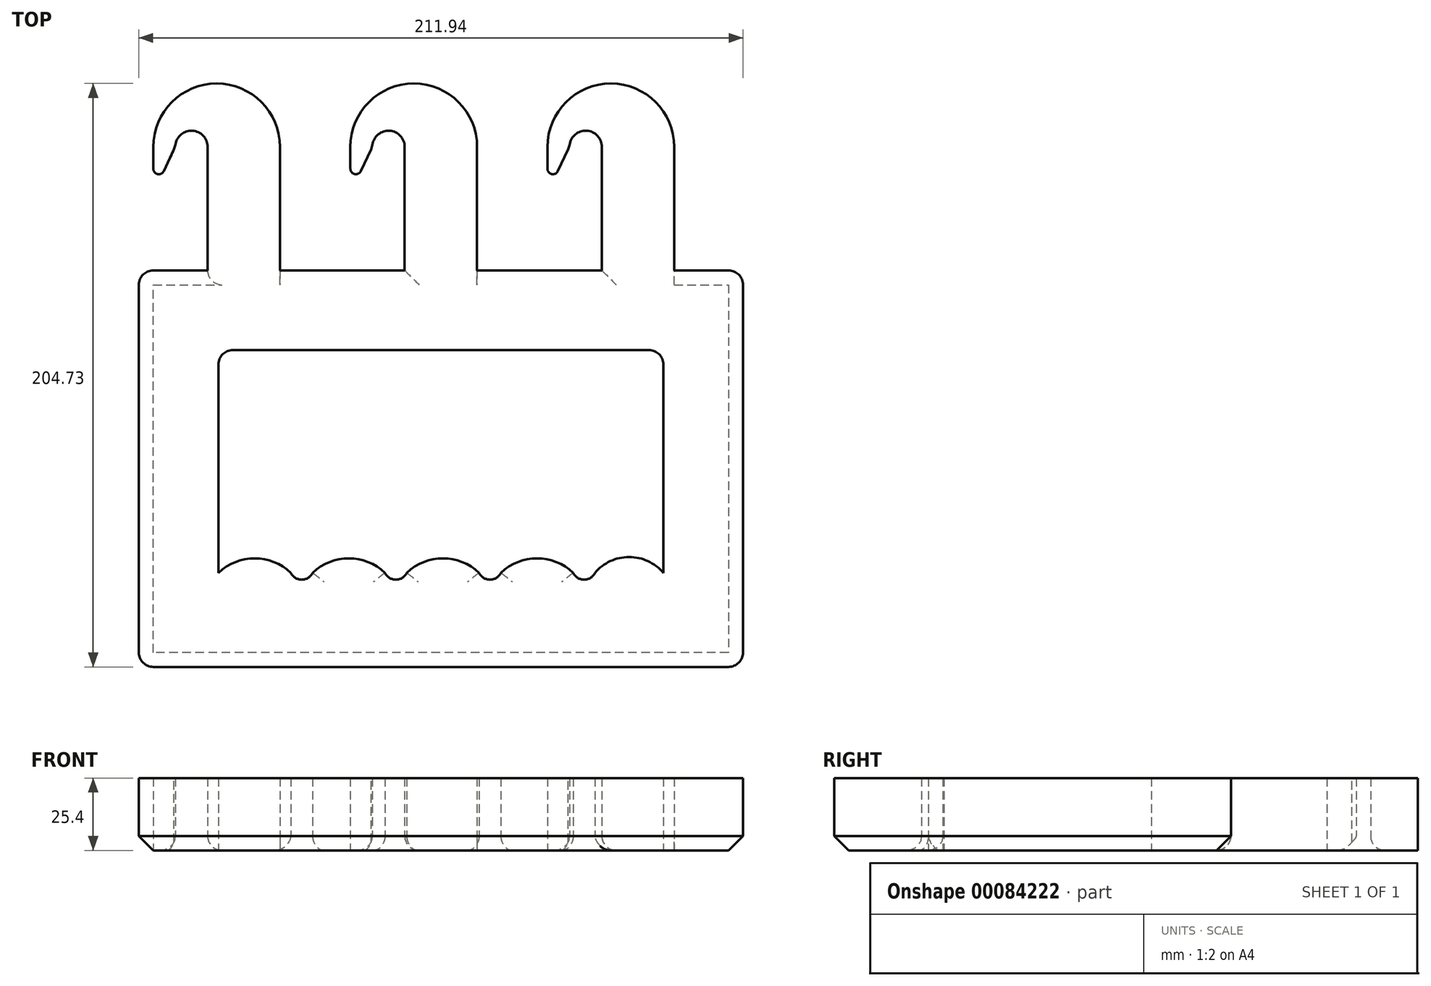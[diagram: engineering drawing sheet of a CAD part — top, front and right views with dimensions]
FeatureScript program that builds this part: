
annotation { "Feature Type Name" : "Feature", "Feature Type Description" : "" }
export const myFeature = defineFeature(function(context is Context, id is Id, definition is map)
    precondition{}
    {
        {
            var Q0;
            Q0=qCreatedBy(makeId("Top.planeOp"),FACE);
            var sketch = newSketch(context, id + "F0", { "sketchPlane" : qUnion([Q0])});
            skLineSegment(sketch, "E0.bottom", {"start": v(80.57, 44.18) * mm, "end": v(-80.57, 44.18) * mm});
            skLineSegment(sketch, "E0.top", {"start": v(80.57, -44.18) * mm, "end": v(-80.57, -44.18) * mm});
            skLineSegment(sketch, "E0.left", {"start": v(80.57, 44.18) * mm, "end": v(80.57, -44.18) * mm});
            skLineSegment(sketch, "E0.right", {"start": v(-80.57, 44.18) * mm, "end": v(-80.57, -44.18) * mm});
            skPoint(sketch, "E0.middle", {"position": v(0, 0) * mm});
            skSolve(sketch);
        }
        {
            var Q0;
            Q0=makeQuery(id+"F0.imprint","IMPRINT",FACE,{"disambiguationData":[TD([[makeQuery(id+"F0.imprint","IMPRINT",EDGE,{"derivedFrom":sQuery(id+"F0.wireOp",EDGE,"E0.bottom")}),1.0]])]});
            extrude(context, id + "F1", {"entities" : qUnion([Q0]), "depth" : 25.4 * mm});
        }
        {
            var Q0;
            Q0=makeQuery(id+"F1.opExtrude","CAP_FACE",FACE,{"disambiguationData":[OSD([sQuery(id+"F0.wireOp",EDGE,"E0.bottom"),sQuery(id+"F0.wireOp",EDGE,"E0.top"),sQuery(id+"F0.wireOp",EDGE,"E0.left"),sQuery(id+"F0.wireOp",EDGE,"E0.right")])],"isStart":true});
            var Q1;
            Q1=makeQuery(id+"F1.opExtrude","CAP_FACE",FACE,{"disambiguationData":[OSD([sQuery(id+"F0.wireOp",EDGE,"E0.bottom"),sQuery(id+"F0.wireOp",EDGE,"E0.top"),sQuery(id+"F0.wireOp",EDGE,"E0.left"),sQuery(id+"F0.wireOp",EDGE,"E0.right")])],"isStart":false});
            shell(context, id + "F2", {"entities" : qUnion([Q0, Q1]), "thickness" : 2.54 * mm});
        }
        {
            var Q0;
            Q0=makeQuery(id+"F1.opExtrude","SWEPT_FACE",FACE,{"disambiguationData":[OSD([sQuery(id+"F0.wireOp",EDGE,"E0.top")])]});
            extrude(context, id + "F3", {"entities" : qUnion([Q0]), "operationType" : NewBodyOperationType.ADD, "depth" : 25.4 * mm});
        }
        {
            var Q0;
            {var subQ0=sQuery(id+"F0.wireOp",EDGE,"E0.left");Q0=makeQuery(id+"F3.boolean.opBoolean","MERGE",FACE,{"derivedFrom":[makeQuery(id+"F1.opExtrude","SWEPT_FACE",FACE,{"disambiguationData":[OSD([subQ0])]}),makeQuery(id+"F3.opExtrude","SWEPT_FACE",FACE,{"disambiguationData":[OSD([sQuery(id+"F0.wireOp",EDGE,"E0.top"),subQ0])]})]});}
            extrude(context, id + "F4", {"entities" : qUnion([Q0]), "operationType" : NewBodyOperationType.ADD, "depth" : 25.4 * mm});
        }
        {
            var Q0;
            {var subQ0=sQuery(id+"F0.wireOp",EDGE,"E0.bottom");Q0=makeQuery(id+"F4.boolean.opBoolean","MERGE",FACE,{"derivedFrom":[makeQuery(id+"F1.opExtrude","SWEPT_FACE",FACE,{"disambiguationData":[OSD([subQ0])]}),makeQuery(id+"F4.opExtrude","SWEPT_FACE",FACE,{"disambiguationData":[OSD([subQ0,sQuery(id+"F0.wireOp",EDGE,"E0.left")])]})]});}
            extrude(context, id + "F5", {"entities" : qUnion([Q0]), "operationType" : NewBodyOperationType.ADD, "depth" : 25.4 * mm});
        }
        {
            var Q0;
            {var subQ0=sQuery(id+"F0.wireOp",EDGE,"E0.right");Q0=makeQuery(id+"F5.boolean.opBoolean","MERGE",FACE,{"derivedFrom":[makeQuery(id+"F3.boolean.opBoolean","MERGE",FACE,{"derivedFrom":[makeQuery(id+"F1.opExtrude","SWEPT_FACE",FACE,{"disambiguationData":[OSD([subQ0])]}),makeQuery(id+"F3.opExtrude","SWEPT_FACE",FACE,{"disambiguationData":[OSD([sQuery(id+"F0.wireOp",EDGE,"E0.top"),subQ0])]})]}),makeQuery(id+"F5.opExtrude","SWEPT_FACE",FACE,{"disambiguationData":[OSD([sQuery(id+"F0.wireOp",EDGE,"E0.bottom"),subQ0])]})]});}
            extrude(context, id + "F6", {"entities" : qUnion([Q0]), "operationType" : NewBodyOperationType.ADD, "depth" : 25.4 * mm});
        }
        {
            var Q0;
            Q0=makeQuery(id+"F6.opExtrude","CAP_EDGE",EDGE,{"disambiguationData":[OSD([sQuery(id+"F0.wireOp",EDGE,"E0.top"),sQuery(id+"F0.wireOp",EDGE,"E0.right")])],"isStart":false});
            var Q1;
            Q1=makeQuery(id+"F2.opShell","OFFSET_EDGE",EDGE,{"disambiguationData":[OSD([sQuery(id+"F0.wireOp",EDGE,"E0.top"),sQuery(id+"F0.wireOp",EDGE,"E0.right")])]});
            var Q2;
            {var subQ0=sQuery(id+"F0.wireOp",EDGE,"E0.left");var subQ1=sQuery(id+"F0.wireOp",EDGE,"E0.bottom");Q2=makeQuery(id+"F5.opExtrude","CAP_EDGE",EDGE,{"disambiguationData":[OSD([subQ1,subQ0]),TDD([makeQuery(id+"F4.opExtrude","CAP_EDGE",EDGE,{"disambiguationData":[OSD([subQ1,subQ0])],"isStart":false})])],"isStart":false});}
            var Q3;
            Q3=makeQuery(id+"F6.opExtrude","CAP_EDGE",EDGE,{"disambiguationData":[OSD([sQuery(id+"F0.wireOp",EDGE,"E0.bottom"),sQuery(id+"F0.wireOp",EDGE,"E0.right")])],"isStart":false});
            var Q4;
            Q4=makeQuery(id+"F2.opShell","OFFSET_EDGE",EDGE,{"disambiguationData":[OSD([sQuery(id+"F0.wireOp",EDGE,"E0.bottom"),sQuery(id+"F0.wireOp",EDGE,"E0.right")])]});
            var Q5;
            Q5=makeQuery(id+"F2.opShell","OFFSET_EDGE",EDGE,{"disambiguationData":[OSD([sQuery(id+"F0.wireOp",EDGE,"E0.bottom"),sQuery(id+"F0.wireOp",EDGE,"E0.left")])]});
            var Q6;
            Q6=makeQuery(id+"F2.opShell","OFFSET_EDGE",EDGE,{"disambiguationData":[OSD([sQuery(id+"F0.wireOp",EDGE,"E0.top"),sQuery(id+"F0.wireOp",EDGE,"E0.left")])]});
            var Q7;
            {var subQ0=sQuery(id+"F0.wireOp",EDGE,"E0.left");var subQ1=sQuery(id+"F0.wireOp",EDGE,"E0.top");Q7=makeQuery(id+"F4.opExtrude","CAP_EDGE",EDGE,{"disambiguationData":[OSD([subQ1,subQ0]),TDD([makeQuery(id+"F3.opExtrude","CAP_EDGE",EDGE,{"disambiguationData":[OSD([subQ1,subQ0])],"isStart":false})])],"isStart":false});}
            fillet(context, id + "F7", {"entities" : qUnion([Q0, Q1, Q2, Q3, Q4, Q5, Q6, Q7]), "radius" : 5.08 * mm, "tangentPropagation" : true, "allowEdgeOverflow" : false});
        }
        {
            var Q0;
            {var subQ0=sQuery(id+"F0.wireOp",EDGE,"E0.right");var subQ1=sQuery(id+"F0.wireOp",EDGE,"E0.left");var subQ2=sQuery(id+"F0.wireOp",EDGE,"E0.top");var subQ3=sQuery(id+"F0.wireOp",EDGE,"E0.bottom");Q0=makeQuery(id+"F4rlxRPwf46HhCo_1.boolean.opBoolean","MERGE",FACE,{"derivedFrom":[makeQuery(id+"F6.boolean.opBoolean","MERGE",FACE,{"derivedFrom":[makeQuery(id+"F5.boolean.opBoolean","MERGE",FACE,{"derivedFrom":[makeQuery(id+"F4.boolean.opBoolean","MERGE",FACE,{"derivedFrom":[makeQuery(id+"F3.boolean.opBoolean","MERGE",FACE,{"derivedFrom":[makeQuery(id+"F1.opExtrude","CAP_FACE",FACE,{"disambiguationData":[OSD([subQ3,subQ2,subQ1,subQ0])],"isStart":true}),makeQuery(id+"F3.opExtrude","SWEPT_FACE",FACE,{"disambiguationData":[OSD([subQ2]),TDD([makeQuery(id+"F1.opExtrude","CAP_EDGE",EDGE,{"disambiguationData":[OSD([subQ2])],"isStart":true})])]})]}),makeQuery(id+"F4.opExtrude","SWEPT_FACE",FACE,{"disambiguationData":[OSD([subQ2,subQ1]),TDD([makeQuery(id+"F3.boolean.opBoolean","MERGE",EDGE,{"derivedFrom":[makeQuery(id+"F1.opExtrude","CAP_EDGE",EDGE,{"disambiguationData":[OSD([subQ1])],"isStart":true}),makeQuery(id+"F3.opExtrude","SWEPT_EDGE",EDGE,{"disambiguationData":[OSD([subQ2,subQ1]),TDD([makeQuery(id+"F1.opExtrude","CAP_VERTEX",VERTEX,{"disambiguationData":[OSD([subQ2,subQ1])],"isStart":true})])]})]})])]})]}),makeQuery(id+"F5.opExtrude","SWEPT_FACE",FACE,{"disambiguationData":[OSD([subQ3,subQ1]),TDD([makeQuery(id+"F4.boolean.opBoolean","MERGE",EDGE,{"derivedFrom":[makeQuery(id+"F1.opExtrude","CAP_EDGE",EDGE,{"disambiguationData":[OSD([subQ3])],"isStart":true}),makeQuery(id+"F4.opExtrude","SWEPT_EDGE",EDGE,{"disambiguationData":[OSD([subQ3,subQ1]),TDD([makeQuery(id+"F1.opExtrude","CAP_VERTEX",VERTEX,{"disambiguationData":[OSD([subQ3,subQ1])],"isStart":true})])]})]})])]})]}),makeQuery(id+"F6.opExtrude","SWEPT_FACE",FACE,{"disambiguationData":[OSD([subQ3,subQ2,subQ0]),TDD([makeQuery(id+"F5.boolean.opBoolean","MERGE",EDGE,{"derivedFrom":[makeQuery(id+"F3.boolean.opBoolean","MERGE",EDGE,{"derivedFrom":[makeQuery(id+"F1.opExtrude","CAP_EDGE",EDGE,{"disambiguationData":[OSD([subQ0])],"isStart":true}),makeQuery(id+"F3.opExtrude","SWEPT_EDGE",EDGE,{"disambiguationData":[OSD([subQ2,subQ0]),TDD([makeQuery(id+"F1.opExtrude","CAP_VERTEX",VERTEX,{"disambiguationData":[OSD([subQ2,subQ0])],"isStart":true})])]})]}),makeQuery(id+"F5.opExtrude","SWEPT_EDGE",EDGE,{"disambiguationData":[OSD([subQ3,subQ0]),TDD([makeQuery(id+"F1.opExtrude","CAP_VERTEX",VERTEX,{"disambiguationData":[OSD([subQ3,subQ0])],"isStart":true})])]})]})])]})]}),makeQuery(id+"F4rlxRPwf46HhCo_1.opExtrude","CAP_FACE",FACE,{"disambiguationData":[OSD([subQ3,subQ2,subQ1,subQ0,sQuery(id+"FdWGWdMTT6Qc4Fu_1.wireOp",EDGE,"d3da10bc-3136-4792-8693-016e846191d0"),sQuery(id+"FdWGWdMTT6Qc4Fu_1.wireOp",EDGE,"aac24d95-50fc-4f8b-b2ee-a3f1f59186e0"),sQuery(id+"FdWGWdMTT6Qc4Fu_1.wireOp",EDGE,"4d405499-a267-42fc-9aab-180142b3633d"),sQuery(id+"FdWGWdMTT6Qc4Fu_1.wireOp",EDGE,"a9ec6842-2591-4f58-a969-2822cd4d4c04"),sQuery(id+"FdWGWdMTT6Qc4Fu_1.wireOp",EDGE,"51de34cb-b12d-4a25-9cfc-016ff7969eb1"),sQuery(id+"FdWGWdMTT6Qc4Fu_1.wireOp",EDGE,"a70d7e88-b675-4396-b805-becb8ebd9cdd"),sQuery(id+"FdWGWdMTT6Qc4Fu_1.wireOp",EDGE,"c629b940-030e-440d-8414-086baef94262"),sQuery(id+"FdWGWdMTT6Qc4Fu_1.wireOp",EDGE,"5c281ef1-6288-44ce-9a01-84a85776ec3e"),sQuery(id+"FdWGWdMTT6Qc4Fu_1.wireOp",EDGE,"403098cf-f73b-4ddd-90e9-7737bff6dcb0")])],"isStart":true})]});}
            var sketch = newSketch(context, id + "F8", { "sketchPlane" : qUnion([Q0])});
            skLineSegment(sketch, "E1.bottom", {"start": v(-81.84, -69.58) * mm, "end": v(-56.44, -69.58) * mm});
            skLineSegment(sketch, "E1.top", {"start": v(-81.84, -112.92) * mm, "end": v(-56.44, -112.92) * mm});
            skLineSegment(sketch, "E1.left", {"start": v(-81.84, -69.58) * mm, "end": v(-81.84, -112.92) * mm});
            skLineSegment(sketch, "E1.right", {"start": v(-56.44, -69.58) * mm, "end": v(-56.44, -112.92) * mm});
            skLineSegment(sketch, "E2.bottom", {"start": v(81.84, -69.58) * mm, "end": v(56.44, -69.58) * mm});
            skLineSegment(sketch, "E2.top", {"start": v(81.84, -112.92) * mm, "end": v(56.44, -112.92) * mm});
            skLineSegment(sketch, "E2.left", {"start": v(81.84, -69.58) * mm, "end": v(81.84, -112.92) * mm});
            skLineSegment(sketch, "E2.right", {"start": v(56.44, -69.58) * mm, "end": v(56.44, -112.92) * mm});
            skLineSegment(sketch, "E3.bottom", {"start": v(-12.7, -69.58) * mm, "end": v(12.7, -69.58) * mm});
            skLineSegment(sketch, "E3.top", {"start": v(-12.7, -112.92) * mm, "end": v(12.7, -112.92) * mm});
            skLineSegment(sketch, "E3.left", {"start": v(-12.7, -69.58) * mm, "end": v(-12.7, -112.92) * mm});
            skLineSegment(sketch, "E3.right", {"start": v(12.7, -69.58) * mm, "end": v(12.7, -112.92) * mm});
            skArc(sketch, "E4", {"start": v(-100.9, -112.92) * mm, "mid": v(-78.67, -135.15) * mm, "end": v(-56.44, -112.92) * mm});
            skArc(sketch, "E5", {"start": v(-31.75, -112.92) * mm, "mid": v(-9.52, -135.15) * mm, "end": v(12.7, -112.92) * mm});
            skArc(sketch, "E6", {"start": v(37.4, -112.92) * mm, "mid": v(59.62, -135.15) * mm, "end": v(81.84, -112.92) * mm});
            skPoint(sketch, "E6.startSnap0", {"position": v(69.14, -112.92) * mm});
            skLineSegment(sketch, "E7", {"start": v(-100.9, -112.92) * mm, "end": v(-100.9, -96.82) * mm});
            skLineSegment(sketch, "E8", {"start": v(-31.75, -112.92) * mm, "end": v(-31.75, -96.82) * mm});
            skLineSegment(sketch, "E9", {"start": v(37.4, -112.92) * mm, "end": v(37.4, -96.82) * mm});
            skLineSegment(sketch, "E10", {"start": v(-100.9, -96.82) * mm, "end": v(-93.19, -112.92) * mm});
            skLineSegment(sketch, "E11", {"start": v(-31.75, -96.82) * mm, "end": v(-24.05, -112.92) * mm});
            skLineSegment(sketch, "E12", {"start": v(37.4, -96.82) * mm, "end": v(45.09, -112.92) * mm});
            skArc(sketch, "E13", {"start": v(-93.19, -112.92) * mm, "mid": v(-87.51, -118.6) * mm, "end": v(-81.84, -112.92) * mm});
            skArc(sketch, "E14", {"start": v(-24.05, -112.92) * mm, "mid": v(-18.37, -118.6) * mm, "end": v(-12.7, -112.92) * mm});
            skArc(sketch, "E15", {"start": v(45.09, -112.92) * mm, "mid": v(50.76, -118.6) * mm, "end": v(56.44, -112.92) * mm});
            skSolve(sketch);
        }
        {
            var Q0;
            Q0=makeQuery(id+"F8.imprint","IMPRINT",FACE,{"disambiguationData":[TD([[makeQuery(id+"F8.imprint","IMPRINT",EDGE,{"derivedFrom":sQuery(id+"F8.wireOp",EDGE,"E1.top")}),-1.0]])]});
            var Q1;
            Q1=makeQuery(id+"F8.imprint","IMPRINT",FACE,{"disambiguationData":[TD([[makeQuery(id+"F8.imprint","IMPRINT",EDGE,{"derivedFrom":sQuery(id+"F8.wireOp",EDGE,"E1.bottom")}),1.0]])]});
            var Q2;
            Q2=makeQuery(id+"F8.imprint","IMPRINT",FACE,{"disambiguationData":[TD([[makeQuery(id+"F8.imprint","IMPRINT",EDGE,{"derivedFrom":sQuery(id+"F8.wireOp",EDGE,"E2.top")}),1.0]])]});
            var Q3;
            Q3=makeQuery(id+"F8.imprint","IMPRINT",FACE,{"disambiguationData":[TD([[makeQuery(id+"F8.imprint","IMPRINT",EDGE,{"derivedFrom":sQuery(id+"F8.wireOp",EDGE,"E3.bottom")}),1.0]])]});
            var Q4;
            Q4=makeQuery(id+"F8.imprint","IMPRINT",FACE,{"disambiguationData":[TD([[makeQuery(id+"F8.imprint","IMPRINT",EDGE,{"derivedFrom":sQuery(id+"F8.wireOp",EDGE,"E2.bottom")}),1.0]])]});
            var Q5;
            Q5=makeQuery(id+"F8.imprint","IMPRINT",FACE,{"disambiguationData":[TD([[makeQuery(id+"F8.imprint","IMPRINT",EDGE,{"derivedFrom":sQuery(id+"F8.wireOp",EDGE,"E3.top")}),-1.0]])]});
            extrude(context, id + "F9", {"entities" : qUnion([Q0, Q1, Q2, Q3, Q4, Q5]), "operationType" : NewBodyOperationType.ADD, "oppositeDirection" : true, "depth" : 25.4 * mm});
        }
        {
            var Q0;
            {var subQ0=sQuery(id+"F0.wireOp",EDGE,"E0.right");var subQ1=sQuery(id+"F0.wireOp",EDGE,"E0.bottom");var subQ2=sQuery(id+"F0.wireOp",EDGE,"E0.top");var subQ3=sQuery(id+"F0.wireOp",EDGE,"E0.left");Q0=makeQuery(id+"F9.boolean.opBoolean","MERGE",FACE,{"derivedFrom":[makeQuery(id+"F6.boolean.opBoolean","MERGE",FACE,{"derivedFrom":[makeQuery(id+"F5.boolean.opBoolean","MERGE",FACE,{"derivedFrom":[makeQuery(id+"F4.boolean.opBoolean","MERGE",FACE,{"derivedFrom":[makeQuery(id+"F3.boolean.opBoolean","MERGE",FACE,{"derivedFrom":[makeQuery(id+"F1.opExtrude","CAP_FACE",FACE,{"disambiguationData":[OSD([subQ1,subQ2,subQ3,subQ0])],"isStart":true}),makeQuery(id+"F3.opExtrude","SWEPT_FACE",FACE,{"disambiguationData":[OSD([subQ2]),TDD([makeQuery(id+"F1.opExtrude","CAP_EDGE",EDGE,{"disambiguationData":[OSD([subQ2])],"isStart":true})])]})]}),makeQuery(id+"F4.opExtrude","SWEPT_FACE",FACE,{"disambiguationData":[OSD([subQ2,subQ3]),TDD([makeQuery(id+"F3.boolean.opBoolean","MERGE",EDGE,{"derivedFrom":[makeQuery(id+"F1.opExtrude","CAP_EDGE",EDGE,{"disambiguationData":[OSD([subQ3])],"isStart":true}),makeQuery(id+"F3.opExtrude","SWEPT_EDGE",EDGE,{"disambiguationData":[OSD([subQ2,subQ3]),TDD([makeQuery(id+"F1.opExtrude","CAP_VERTEX",VERTEX,{"disambiguationData":[OSD([subQ2,subQ3])],"isStart":true})])]})]})])]})]}),makeQuery(id+"F5.opExtrude","SWEPT_FACE",FACE,{"disambiguationData":[OSD([subQ1,subQ3]),TDD([makeQuery(id+"F4.boolean.opBoolean","MERGE",EDGE,{"derivedFrom":[makeQuery(id+"F1.opExtrude","CAP_EDGE",EDGE,{"disambiguationData":[OSD([subQ1])],"isStart":true}),makeQuery(id+"F4.opExtrude","SWEPT_EDGE",EDGE,{"disambiguationData":[OSD([subQ1,subQ3]),TDD([makeQuery(id+"F1.opExtrude","CAP_VERTEX",VERTEX,{"disambiguationData":[OSD([subQ1,subQ3])],"isStart":true})])]})]})])]})]}),makeQuery(id+"F6.opExtrude","SWEPT_FACE",FACE,{"disambiguationData":[OSD([subQ1,subQ2,subQ0]),TDD([makeQuery(id+"F5.boolean.opBoolean","MERGE",EDGE,{"derivedFrom":[makeQuery(id+"F3.boolean.opBoolean","MERGE",EDGE,{"derivedFrom":[makeQuery(id+"F1.opExtrude","CAP_EDGE",EDGE,{"disambiguationData":[OSD([subQ0])],"isStart":true}),makeQuery(id+"F3.opExtrude","SWEPT_EDGE",EDGE,{"disambiguationData":[OSD([subQ2,subQ0]),TDD([makeQuery(id+"F1.opExtrude","CAP_VERTEX",VERTEX,{"disambiguationData":[OSD([subQ2,subQ0])],"isStart":true})])]})]}),makeQuery(id+"F5.opExtrude","SWEPT_EDGE",EDGE,{"disambiguationData":[OSD([subQ1,subQ0]),TDD([makeQuery(id+"F1.opExtrude","CAP_VERTEX",VERTEX,{"disambiguationData":[OSD([subQ1,subQ0])],"isStart":true})])]})]})])]})]}),makeQuery(id+"F9.opExtrude","CAP_FACE",FACE,{"disambiguationData":[OSD([sQuery(id+"F8.wireOp",EDGE,"E1.bottom"),sQuery(id+"F8.wireOp",EDGE,"E1.left"),sQuery(id+"F8.wireOp",EDGE,"E1.right"),sQuery(id+"F8.wireOp",EDGE,"E4"),sQuery(id+"F8.wireOp",EDGE,"E7"),sQuery(id+"F8.wireOp",EDGE,"E10"),sQuery(id+"F8.wireOp",EDGE,"E13")])],"isStart":true}),makeQuery(id+"F9.opExtrude","CAP_FACE",FACE,{"disambiguationData":[OSD([sQuery(id+"F8.wireOp",EDGE,"E2.bottom"),sQuery(id+"F8.wireOp",EDGE,"E2.left"),sQuery(id+"F8.wireOp",EDGE,"E2.right"),sQuery(id+"F8.wireOp",EDGE,"E6"),sQuery(id+"F8.wireOp",EDGE,"E9"),sQuery(id+"F8.wireOp",EDGE,"E12"),sQuery(id+"F8.wireOp",EDGE,"E15")])],"isStart":true}),makeQuery(id+"F9.opExtrude","CAP_FACE",FACE,{"disambiguationData":[OSD([sQuery(id+"F8.wireOp",EDGE,"E3.bottom"),sQuery(id+"F8.wireOp",EDGE,"E3.left"),sQuery(id+"F8.wireOp",EDGE,"E3.right"),sQuery(id+"F8.wireOp",EDGE,"E5"),sQuery(id+"F8.wireOp",EDGE,"E8"),sQuery(id+"F8.wireOp",EDGE,"E11"),sQuery(id+"F8.wireOp",EDGE,"E14")])],"isStart":true})]});}
            var sketch = newSketch(context, id + "F10", { "sketchPlane" : qUnion([Q0])});
            skArc(sketch, "E16", {"start": v(-78.03, 36.56) * mm, "mid": v(-65.33, 31.48) * mm, "end": v(-52.63, 36.56) * mm});
            skArc(sketch, "E17", {"start": v(-45.01, 36.56) * mm, "mid": v(-48.82, 38.98) * mm, "end": v(-52.63, 36.56) * mm});
            skArc(sketch, "E18", {"start": v(-45.01, 36.56) * mm, "mid": v(-32.31, 31.48) * mm, "end": v(-19.61, 36.56) * mm});
            skArc(sketch, "E19", {"start": v(-12, 36.56) * mm, "mid": v(-15.8, 38.98) * mm, "end": v(-19.61, 36.56) * mm});
            skArc(sketch, "E20", {"start": v(-12, 36.56) * mm, "mid": v(0.7, 31.48) * mm, "end": v(13.4, 36.56) * mm});
            skArc(sketch, "E21", {"start": v(21.03, 36.56) * mm, "mid": v(17.22, 38.98) * mm, "end": v(13.4, 36.56) * mm});
            skArc(sketch, "E22", {"start": v(21.03, 36.56) * mm, "mid": v(33.73, 31.48) * mm, "end": v(46.43, 36.56) * mm});
            skArc(sketch, "E23", {"start": v(54.05, 36.56) * mm, "mid": v(50.24, 38.98) * mm, "end": v(46.43, 36.56) * mm});
            skArc(sketch, "E24", {"start": v(54.05, 36.56) * mm, "mid": v(66.04, 31.03) * mm, "end": v(78.03, 36.56) * mm});
            skSolve(sketch);
        }
        {
            var Q0;
            Q0=makeQuery(id+"F10.imprint","IMPRINT",FACE,{"disambiguationData":[TD([[makeQuery(id+"F10.imprint","IMPRINT",EDGE,{"derivedFrom":sQuery(id+"F10.wireOp",EDGE,"E16")}),1.0]])]});
            extrude(context, id + "F11", {"entities" : qUnion([Q0]), "operationType" : NewBodyOperationType.ADD, "oppositeDirection" : true, "depth" : 25.4 * mm});
        }
        {
            var Q0;
            Q0=makeQuery(id+"F11.opExtrude","CAP_EDGE",EDGE,{"disambiguationData":[OSD([sQuery(id+"F10.wireOp",EDGE,"E17")])],"isStart":true});
            var Q1;
            Q1=makeQuery(id+"F11.opExtrude","CAP_EDGE",EDGE,{"disambiguationData":[OSD([sQuery(id+"F10.wireOp",EDGE,"E18")])],"isStart":true});
            var Q2;
            Q2=makeQuery(id+"F11.opExtrude","CAP_EDGE",EDGE,{"disambiguationData":[OSD([sQuery(id+"F10.wireOp",EDGE,"E19")])],"isStart":true});
            var Q3;
            Q3=makeQuery(id+"F11.opExtrude","CAP_EDGE",EDGE,{"disambiguationData":[OSD([sQuery(id+"F10.wireOp",EDGE,"E20")])],"isStart":true});
            var Q4;
            Q4=makeQuery(id+"F11.opExtrude","CAP_EDGE",EDGE,{"disambiguationData":[OSD([sQuery(id+"F10.wireOp",EDGE,"E21")])],"isStart":true});
            var Q5;
            Q5=makeQuery(id+"F11.opExtrude","CAP_EDGE",EDGE,{"disambiguationData":[OSD([sQuery(id+"F10.wireOp",EDGE,"E22")])],"isStart":true});
            var Q6;
            Q6=makeQuery(id+"F11.opExtrude","CAP_EDGE",EDGE,{"disambiguationData":[OSD([sQuery(id+"F10.wireOp",EDGE,"E23")])],"isStart":true});
            fillet(context, id + "F12", {"entities" : qUnion([Q0, Q1, Q2, Q3, Q4, Q5, Q6]), "radius" : 5.08 * mm, "tangentPropagation" : true, "allowEdgeOverflow" : false});
        }
        {
            var Q0;
            Q0=makeQuery(id+"F9.opExtrude","SWEPT_EDGE",EDGE,{"disambiguationData":[OSD([sQuery(id+"F8.wireOp",EDGE,"E7"),sQuery(id+"F8.wireOp",EDGE,"E10")])]});
            var Q1;
            Q1=makeQuery(id+"F9.opExtrude","SWEPT_EDGE",EDGE,{"disambiguationData":[OSD([sQuery(id+"F8.wireOp",EDGE,"E8"),sQuery(id+"F8.wireOp",EDGE,"E11")])]});
            var Q2;
            Q2=makeQuery(id+"F9.opExtrude","SWEPT_EDGE",EDGE,{"disambiguationData":[OSD([sQuery(id+"F8.wireOp",EDGE,"E9"),sQuery(id+"F8.wireOp",EDGE,"E12")])]});
            fillet(context, id + "F13", {"entities" : qUnion([Q0, Q1, Q2]), "radius" : 1.9 * mm, "tangentPropagation" : true, "allowEdgeOverflow" : false});
        }
        {
            var Q0;
            Q0=makeQuery(id+"F9.opExtrude","SWEPT_EDGE",EDGE,{"disambiguationData":[OSD([sQuery(id+"F8.wireOp",EDGE,"E11"),sQuery(id+"F8.wireOp",EDGE,"E14")])]});
            var Q1;
            Q1=makeQuery(id+"F9.opExtrude","SWEPT_EDGE",EDGE,{"disambiguationData":[OSD([sQuery(id+"F8.wireOp",EDGE,"E12"),sQuery(id+"F8.wireOp",EDGE,"E15")])]});
            var Q2;
            Q2=makeQuery(id+"F9.opExtrude","SWEPT_EDGE",EDGE,{"disambiguationData":[OSD([sQuery(id+"F8.wireOp",EDGE,"E10"),sQuery(id+"F8.wireOp",EDGE,"E13")])]});
            chamfer(context, id + "F14", {"entities" : qUnion([Q0, Q1, Q2]), "width" : 5.08 * mm, "tangentPropagation" : true});
        }
        {
            var Q0;
            {var subQ0=sQuery(id+"F0.wireOp",EDGE,"E0.right");var subQ1=sQuery(id+"F0.wireOp",EDGE,"E0.top");var subQ2=sQuery(id+"F0.wireOp",EDGE,"E0.left");Q0=makeQuery(id+"F6.boolean.opBoolean","MERGE",EDGE,{"derivedFrom":[makeQuery(id+"F4.boolean.opBoolean","MERGE",EDGE,{"derivedFrom":[makeQuery(id+"F3.opExtrude","CAP_EDGE",EDGE,{"disambiguationData":[OSD([subQ1]),TDD([makeQuery(id+"F1.opExtrude","CAP_EDGE",EDGE,{"disambiguationData":[OSD([subQ1])],"isStart":true})])],"isStart":false}),makeQuery(id+"F4.opExtrude","SWEPT_EDGE",EDGE,{"disambiguationData":[OSD([subQ1,subQ2]),TDD([makeQuery(id+"F3.opExtrude","CAP_VERTEX",VERTEX,{"disambiguationData":[OSD([subQ1,subQ2]),TDD([makeQuery(id+"F1.opExtrude","CAP_VERTEX",VERTEX,{"disambiguationData":[OSD([subQ1,subQ2])],"isStart":true})])],"isStart":false})])]})]}),makeQuery(id+"F6.opExtrude","SWEPT_EDGE",EDGE,{"disambiguationData":[OSD([subQ1,subQ0]),TDD([makeQuery(id+"F3.opExtrude","CAP_VERTEX",VERTEX,{"disambiguationData":[OSD([subQ1,subQ0]),TDD([makeQuery(id+"F1.opExtrude","CAP_VERTEX",VERTEX,{"disambiguationData":[OSD([subQ1,subQ0])],"isStart":true})])],"isStart":false})])]})]});}
            chamfer(context, id + "F15", {"entities" : qUnion([Q0]), "width" : 5.08 * mm, "tangentPropagation" : true});
        }
        {
            var Q0;
            Q0=makeQuery(id+"F9.opExtrude","CAP_EDGE",EDGE,{"disambiguationData":[OSD([sQuery(id+"F8.wireOp",EDGE,"E1.left")])],"isStart":true});
            var Q1;
            Q1=makeQuery(id+"F9.opExtrude","CAP_EDGE",EDGE,{"disambiguationData":[OSD([sQuery(id+"F8.wireOp",EDGE,"E3.left")])],"isStart":true});
            var Q2;
            Q2=makeQuery(id+"F9.opExtrude","CAP_EDGE",EDGE,{"disambiguationData":[OSD([sQuery(id+"F8.wireOp",EDGE,"E2.right")])],"isStart":true});
            var Q3;
            {var subQ0=sQuery(id+"F8.wireOp",EDGE,"E2.right");var subQ1=sQuery(id+"F0.wireOp",EDGE,"E0.right");var subQ2=sQuery(id+"F0.wireOp",EDGE,"E0.bottom");var subQ3=makeQuery(id+"F1.opExtrude","CAP_VERTEX",VERTEX,{"disambiguationData":[OSD([subQ2,subQ1])],"isStart":true});var subQ5=sQuery(id+"F0.wireOp",EDGE,"E0.left");var subQ6=makeQuery(id+"F4.boolean.opBoolean","MERGE",EDGE,{"derivedFrom":[makeQuery(id+"F1.opExtrude","CAP_EDGE",EDGE,{"disambiguationData":[OSD([subQ2])],"isStart":true}),makeQuery(id+"F4.opExtrude","SWEPT_EDGE",EDGE,{"disambiguationData":[OSD([subQ2,subQ5]),TDD([makeQuery(id+"F1.opExtrude","CAP_VERTEX",VERTEX,{"disambiguationData":[OSD([subQ2,subQ5])],"isStart":true})])]})]});Q3=makeQuery(id+"F9.boolean.opBoolean","SPLIT",EDGE,{"disambiguationData":[TD([makeQuery(id+"F9.opExtrude","SWEPT_FACE",FACE,{"disambiguationData":[OSD([subQ0])]})])],"derivedFrom":makeQuery(id+"F6.boolean.opBoolean","MERGE",EDGE,{"derivedFrom":[makeQuery(id+"F5.opExtrude","CAP_EDGE",EDGE,{"disambiguationData":[OSD([subQ2,subQ5]),TDD([subQ6])],"isStart":false}),makeQuery(id+"F6.opExtrude","SWEPT_EDGE",EDGE,{"disambiguationData":[OSD([subQ2,subQ1]),TDD([makeQuery(id+"F5.opExtrude","CAP_VERTEX",VERTEX,{"disambiguationData":[OSD([subQ2,subQ1]),TDD([subQ3])],"isStart":false})])]})]})});}
            var Q4;
            {var subQ0=sQuery(id+"F8.wireOp",EDGE,"E1.right");var subQ2=sQuery(id+"F0.wireOp",EDGE,"E0.right");var subQ3=sQuery(id+"F0.wireOp",EDGE,"E0.bottom");var subQ4=makeQuery(id+"F1.opExtrude","CAP_VERTEX",VERTEX,{"disambiguationData":[OSD([subQ3,subQ2])],"isStart":true});var subQ6=sQuery(id+"F0.wireOp",EDGE,"E0.left");var subQ7=makeQuery(id+"F4.boolean.opBoolean","MERGE",EDGE,{"derivedFrom":[makeQuery(id+"F1.opExtrude","CAP_EDGE",EDGE,{"disambiguationData":[OSD([subQ3])],"isStart":true}),makeQuery(id+"F4.opExtrude","SWEPT_EDGE",EDGE,{"disambiguationData":[OSD([subQ3,subQ6]),TDD([makeQuery(id+"F1.opExtrude","CAP_VERTEX",VERTEX,{"disambiguationData":[OSD([subQ3,subQ6])],"isStart":true})])]})]});Q4=makeQuery(id+"F9.boolean.opBoolean","SPLIT",EDGE,{"disambiguationData":[TD([makeQuery(id+"F9.opExtrude","SWEPT_FACE",FACE,{"disambiguationData":[OSD([subQ0])]})])],"derivedFrom":makeQuery(id+"F6.boolean.opBoolean","MERGE",EDGE,{"derivedFrom":[makeQuery(id+"F5.opExtrude","CAP_EDGE",EDGE,{"disambiguationData":[OSD([subQ3,subQ6]),TDD([subQ7])],"isStart":false}),makeQuery(id+"F6.opExtrude","SWEPT_EDGE",EDGE,{"disambiguationData":[OSD([subQ3,subQ2]),TDD([makeQuery(id+"F5.opExtrude","CAP_VERTEX",VERTEX,{"disambiguationData":[OSD([subQ3,subQ2]),TDD([subQ4])],"isStart":false})])]})]})});}
            fillet(context, id + "F16", {"entities" : qUnion([Q0, Q1, Q2, Q3, Q4]), "radius" : 5.08 * mm, "tangentPropagation" : true, "allowEdgeOverflow" : false});
        }
    });
